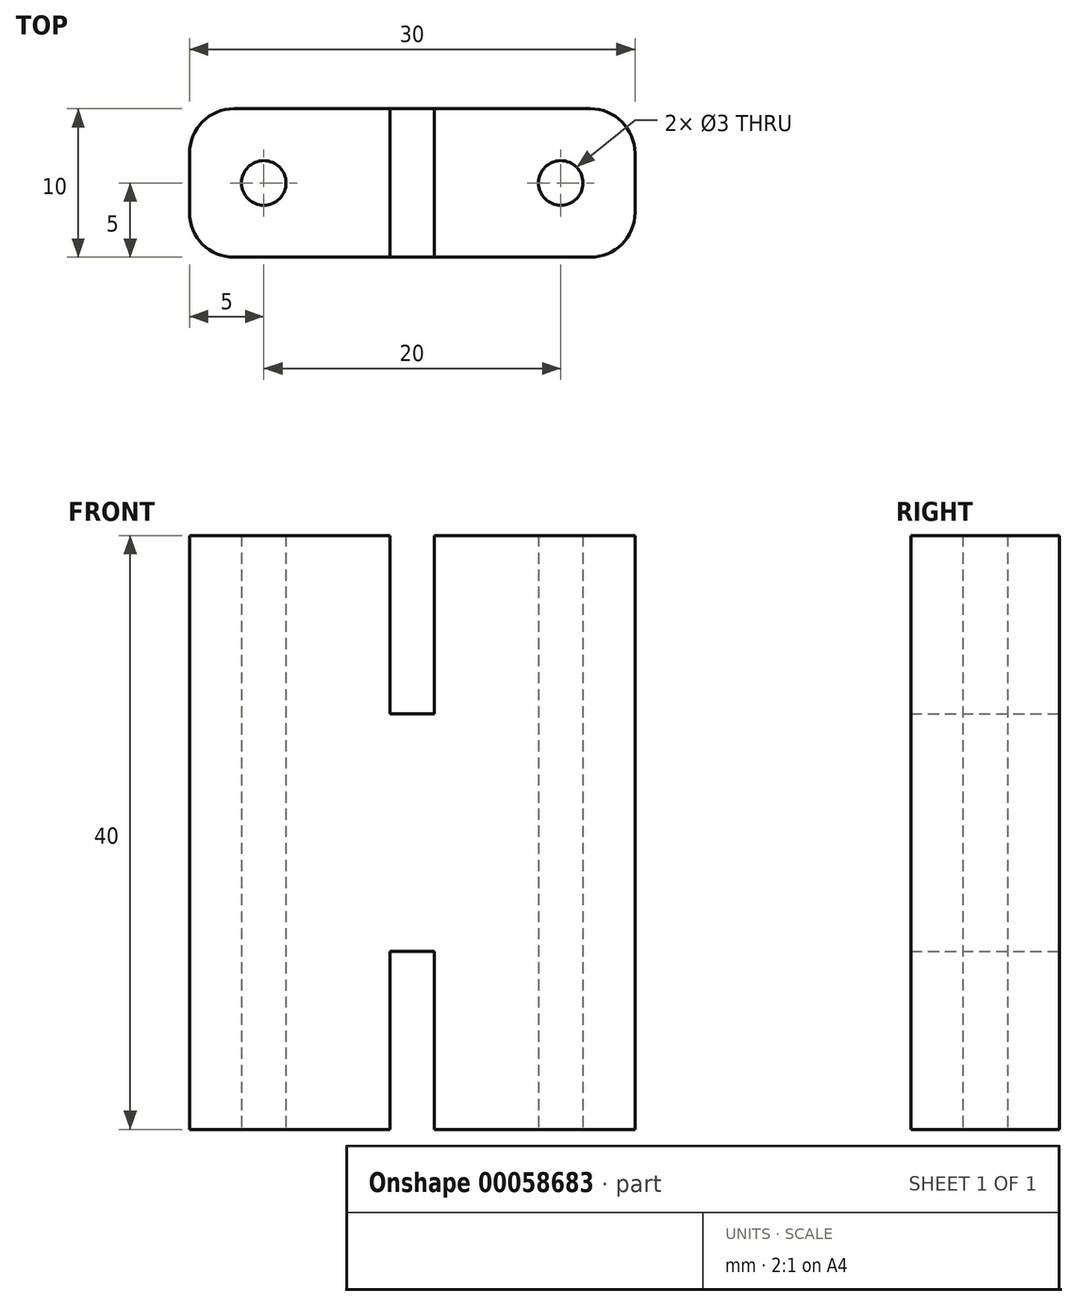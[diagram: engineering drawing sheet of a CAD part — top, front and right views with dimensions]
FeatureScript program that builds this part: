
annotation { "Feature Type Name" : "Feature", "Feature Type Description" : "" }
export const myFeature = defineFeature(function(context is Context, id is Id, definition is map)
    precondition{}
    {
        {
            var Q0;
            Q0=qCreatedBy(makeId("Top.planeOp"),FACE);
            var sketch = newSketch(context, id + "F0", { "sketchPlane" : qUnion([Q0])});
            skCircle(sketch, "E0", {"center": v(10, 0) * mm, "radius": 1.5 * mm});
            skLineSegment(sketch, "E1.rect.bottom", {"start": v(12, 5) * mm, "end": v(-12, 5) * mm});
            skLineSegment(sketch, "E1.rect.top", {"start": v(12, -5) * mm, "end": v(-12, -5) * mm});
            skLineSegment(sketch, "E1.rect.left", {"start": v(15, 2) * mm, "end": v(15, -2) * mm});
            skLineSegment(sketch, "E1.rect.right", {"start": v(-15, 2) * mm, "end": v(-15, -2) * mm});
            skPoint(sketch, "E1.rect.middle", {"position": v(0, 0) * mm});
            skLineSegment(sketch, "E2", {"start": v(0, 5) * mm, "end": v(0, -5) * mm, "construction": true});
            skCircle(sketch, "E3.MirrorC", {"center": v(-10, 0) * mm, "radius": 1.5 * mm});
            skPoint(sketch, "E4.visualSharp", {"position": v(-15, 5) * mm});
            skArc(sketch, "E4.filletArc", {"start": v(-12, 5) * mm, "mid": v(-14.12, 4.12) * mm, "end": v(-15, 2) * mm});
            skPoint(sketch, "E5.visualSharp", {"position": v(15, 5) * mm});
            skArc(sketch, "E5.filletArc", {"start": v(15, 2) * mm, "mid": v(14.12, 4.12) * mm, "end": v(12, 5) * mm});
            skPoint(sketch, "E6.visualSharp", {"position": v(-15, -5) * mm});
            skArc(sketch, "E6.filletArc", {"start": v(-15, -2) * mm, "mid": v(-14.12, -4.12) * mm, "end": v(-12, -5) * mm});
            skPoint(sketch, "E7.visualSharp", {"position": v(15, -5) * mm});
            skArc(sketch, "E7.filletArc", {"start": v(12, -5) * mm, "mid": v(14.12, -4.12) * mm, "end": v(15, -2) * mm});
            skSolve(sketch);
        }
        {
            var Q0;
            Q0 = qSketchRegion(id + "F0", true);
            extrude(context, id + "F1", {"entities" : qUnion([Q0]), "depth" : 20 * mm});
        }
        {
            var Q0;
            Q0=makeQuery(id+"F1.opExtrude","CAP_FACE",FACE,{"disambiguationData":[OSD([sQuery(id+"F0.wireOp",EDGE,"E0"),sQuery(id+"F0.wireOp",EDGE,"E1.rect.bottom"),sQuery(id+"F0.wireOp",EDGE,"E1.rect.top"),sQuery(id+"F0.wireOp",EDGE,"E1.rect.left"),sQuery(id+"F0.wireOp",EDGE,"E1.rect.right"),sQuery(id+"F0.wireOp",EDGE,"E3.MirrorC"),sQuery(id+"F0.wireOp",EDGE,"E4.filletArc"),sQuery(id+"F0.wireOp",EDGE,"E5.filletArc"),sQuery(id+"F0.wireOp",EDGE,"E6.filletArc"),sQuery(id+"F0.wireOp",EDGE,"E7.filletArc")])],"isStart":true});
            var sketch = newSketch(context, id + "F2", { "sketchPlane" : qUnion([Q0])});
            skLineSegment(sketch, "E8.rect.bottom", {"start": v(1.5, 5) * mm, "end": v(-1.5, 5) * mm});
            skLineSegment(sketch, "E8.rect.top", {"start": v(1.5, -5) * mm, "end": v(-1.5, -5) * mm});
            skLineSegment(sketch, "E8.rect.left", {"start": v(1.5, 5) * mm, "end": v(1.5, -5) * mm});
            skLineSegment(sketch, "E8.rect.right", {"start": v(-1.5, 5) * mm, "end": v(-1.5, -5) * mm});
            skPoint(sketch, "E8.rect.middle", {"position": v(0, 0) * mm});
            skSolve(sketch);
        }
        {
            var Q0;
            Q0 = qSketchRegion(id + "F2", true);
            extrude(context, id + "F3", {"entities" : qUnion([Q0]), "operationType" : NewBodyOperationType.REMOVE, "oppositeDirection" : true, "depth" : 12 * mm});
        }
        {
            var Q0;
            Q0=makeQuery(id+"F1.opExtrude","SWEPT_BODY",BODY,{"disambiguationData":[OSD([sQuery(id+"F0.wireOp",EDGE,"E0"),sQuery(id+"F0.wireOp",EDGE,"E1.rect.bottom"),sQuery(id+"F0.wireOp",EDGE,"E1.rect.top"),sQuery(id+"F0.wireOp",EDGE,"E1.rect.left"),sQuery(id+"F0.wireOp",EDGE,"E1.rect.right"),sQuery(id+"F0.wireOp",EDGE,"E3.MirrorC"),sQuery(id+"F0.wireOp",EDGE,"E4.filletArc"),sQuery(id+"F0.wireOp",EDGE,"E5.filletArc"),sQuery(id+"F0.wireOp",EDGE,"E6.filletArc"),sQuery(id+"F0.wireOp",EDGE,"E7.filletArc")])]});
            var Q1;
            Q1=makeQuery(id+"F1.opExtrude","CAP_FACE",FACE,{"disambiguationData":[OSD([sQuery(id+"F0.wireOp",EDGE,"E0"),sQuery(id+"F0.wireOp",EDGE,"E1.rect.bottom"),sQuery(id+"F0.wireOp",EDGE,"E1.rect.top"),sQuery(id+"F0.wireOp",EDGE,"E1.rect.left"),sQuery(id+"F0.wireOp",EDGE,"E1.rect.right"),sQuery(id+"F0.wireOp",EDGE,"E3.MirrorC"),sQuery(id+"F0.wireOp",EDGE,"E4.filletArc"),sQuery(id+"F0.wireOp",EDGE,"E5.filletArc"),sQuery(id+"F0.wireOp",EDGE,"E6.filletArc"),sQuery(id+"F0.wireOp",EDGE,"E7.filletArc")])],"isStart":false});
            mirror(context, id + "F4", {"operationType" : NewBodyOperationType.ADD, "entities" : qUnion([Q0]), "mirrorPlane" : qUnion([Q1])});
        }
    });
